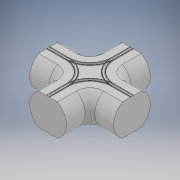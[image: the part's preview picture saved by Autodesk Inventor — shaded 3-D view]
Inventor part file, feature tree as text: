
AUTODESK INVENTOR PART (.ipt)
format: ipt  version: 2017 (Build 210142000, 142)  size: 461,824 bytes
history: native  units: in
note: dims shown in document units (in); Inventor stores cm internally (conversion verified against a paired STEP export)
features: sketch x6, extrude x3, mirror x3, plane x1, sweep x1, other x1
ambient origin geometry x8: Origin, YZ Plane, XZ Plane, XY Plane, X Axis, Y Axis, Z Axis, Center Point
bodies: Body1 (feature_tree)
feature tree (15):
  sketch  "Sketch1"  dims[d0=6.6667in d2=9.7746in d5=-4.8873in d62=45.0deg d71=4.0in d72=0.0in]
  extrude  "corridor eighth"  Depth=4.0in TaperAngle=45.0deg
  plane  "Work Plane1"
  sketch  "Sketch17"  dims[d170=10.3167in d171=10.3167in]
  sketch  "Sketch7"  dims[d160=4.0in d168=10.3167in d169=10.3167in]
  sweep  "Sweep4"
  mirror  "mirror plane YZ"
  extrude  "corridor eighth complete"  Depth=10.3167in
  mirror  "Mirror half"
  mirror  "Mirrorfull"
  extrude  "hole fill in"  Depth=0.0625in
  other  "corridor"
  sketch  "Sketch22"  dims[d196=4.0in d197=0.5833in d198=3.8873in d199=3.8873in d200=1.7083in d201=0.0625in d202=0.0625in d203=1.6458in d204=0.25in d205=0.125in d206=0.0892in d207=0.0884in d208=45.0deg d209=3.3333in d210=0.125in d211=1.0in]
  sketch  "Sketch23"  dims[d212=0.0in d213=0.0in]
  sketch  "Sketch24"  dims[d214=4.0in d215=0.0in d216=4.0in d217=0.0in]
